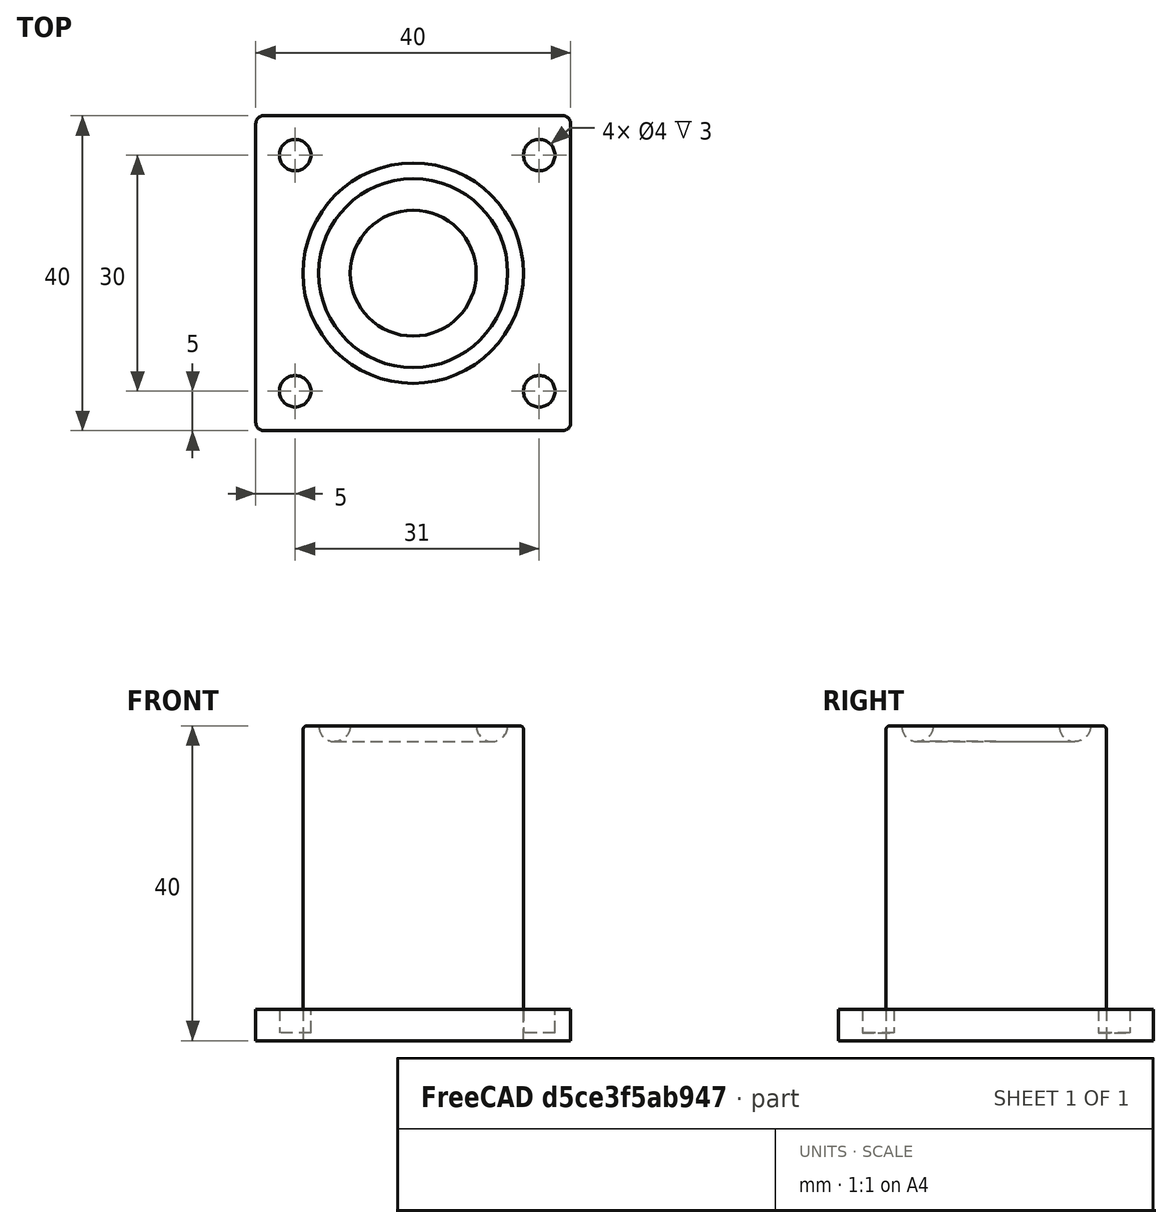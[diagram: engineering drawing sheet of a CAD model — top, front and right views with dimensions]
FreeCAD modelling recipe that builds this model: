
FCSTD DOCUMENT  (FreeCAD 0.21R33694 (Git))
Label: OJT1_T15R03_pota
License: All rights reserved
LicenseURL: http://en.wikipedia.org/wiki/All_rights_reserved
objects: Part::Cylinder×5, Part::Cut×5, Part::Fillet×2, Part::Box×1, Part::Torus×1
note: 14 computed .brp shape members not serialized (recipe doc carries the construction recipe); baked Part::Feature solids carry a one-line shape summary decoded from their .brp

FEATURE [Part::Box] Box  label="Cube"
  AttacherType = Attacher::AttachEngine3D
  Height = 4
  Length = 40
  Width = 40
FEATURE [Part::Fillet] Fillet
  Base = -> Box
  Edges = 4 edges r=1: [Edge1,Edge3,Edge5,Edge7]
FEATURE [Part::Cylinder] Cylinder
  Angle = 360
  AttacherType = Attacher::AttachEngine3D
  FirstAngle = 0
  Height = 4
  Placement = pos=(36,5,1) rot=(0,0,1;0rad)
  Radius = 2
  SecondAngle = 0
FEATURE [Part::Cylinder] Cylinder001
  Angle = 360
  AttacherType = Attacher::AttachEngine3D
  FirstAngle = 0
  Height = 4
  Placement = pos=(5,5,1) rot=(0,0,1;0rad)
  Radius = 2
  SecondAngle = 0
FEATURE [Part::Cylinder] Cylinder002
  Angle = 360
  AttacherType = Attacher::AttachEngine3D
  FirstAngle = 0
  Height = 4
  Placement = pos=(5,35,1) rot=(0,0,1;0rad)
  Radius = 2
  SecondAngle = 0
FEATURE [Part::Cylinder] Cylinder003
  Angle = 360
  AttacherType = Attacher::AttachEngine3D
  FirstAngle = 0
  Height = 4
  Placement = pos=(36,35,1) rot=(0,0,1;0rad)
  Radius = 2
  SecondAngle = 0
FEATURE [Part::Cylinder] Cylinder004
  Angle = 360
  AttacherType = Attacher::AttachEngine3D
  FirstAngle = 0
  Height = 40
  Placement = pos=(20,20,0) rot=(0,0,1;0rad)
  Radius = 14
  SecondAngle = 0
FEATURE [Part::Torus] Torus
  Angle1 = -180
  Angle2 = 180
  Angle3 = 360
  AttacherType = Attacher::AttachEngine3D
  Placement = pos=(20,20,40) rot=(0,0,1;0rad)
  Radius1 = 10
  Radius2 = 2
FEATURE [Part::Cut] Cut
  Base = -> Cylinder004
  Refine = true
  Tool = -> Torus
FEATURE [Part::Fillet] Fillet001
  Base = -> Cut
  Edges = 1 edges r=0.5: [Edge3]
FEATURE [Part::Cut] Cut001
  Base = -> Fillet
  Refine = true
  Tool = -> Cylinder
FEATURE [Part::Cut] Cut002
  Base = -> Cut001
  Refine = true
  Tool = -> Cylinder001
FEATURE [Part::Cut] Cut003
  Base = -> Cut002
  Refine = true
  Tool = -> Cylinder002
FEATURE [Part::Cut] Cut004
  Base = -> Cut003
  Refine = true
  Tool = -> Cylinder003
